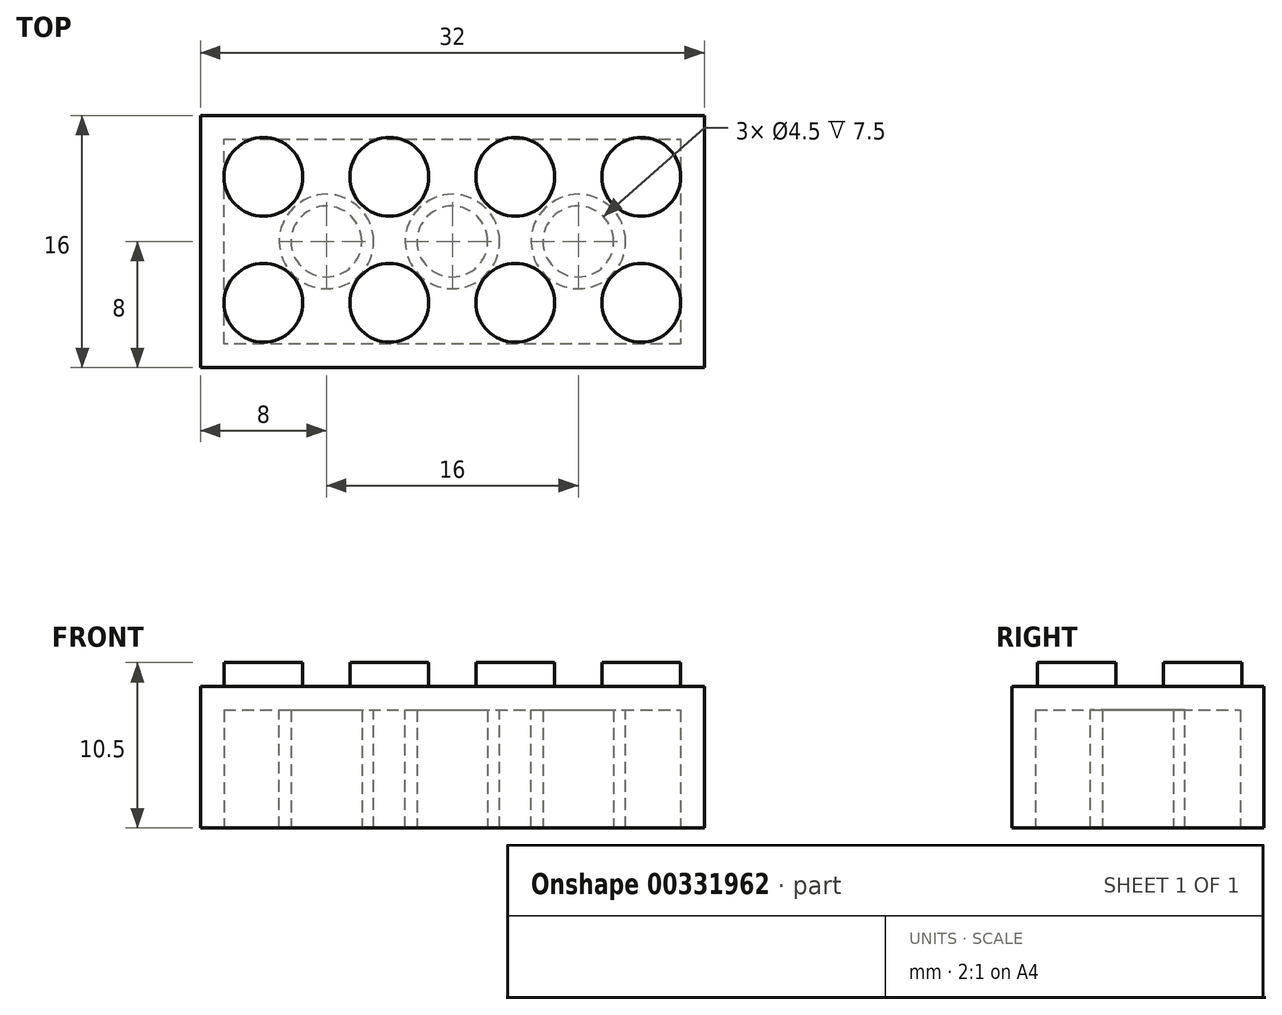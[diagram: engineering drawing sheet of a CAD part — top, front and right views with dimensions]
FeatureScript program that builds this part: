
annotation { "Feature Type Name" : "Feature", "Feature Type Description" : "" }
export const myFeature = defineFeature(function(context is Context, id is Id, definition is map)
    precondition{}
    {
        {
            var Q0;
            Q0=qCreatedBy(makeId("Top.planeOp"),FACE);
            var sketch = newSketch(context, id + "F0", { "sketchPlane" : qUnion([Q0])});
            skLineSegment(sketch, "E0.bottom", {"start": v(0, 0) * mm, "end": v(32, 0) * mm});
            skLineSegment(sketch, "E0.top", {"start": v(0, 16) * mm, "end": v(32, 16) * mm});
            skLineSegment(sketch, "E0.left", {"start": v(0, 0) * mm, "end": v(0, 16) * mm});
            skLineSegment(sketch, "E0.right", {"start": v(32, 0) * mm, "end": v(32, 16) * mm});
            skSolve(sketch);
        }
        {
            var Q0;
            Q0=makeQuery(id+"F0.imprint","IMPRINT",FACE,{"disambiguationData":[TD([[makeQuery(id+"F0.imprint","IMPRINT",EDGE,{"derivedFrom":sQuery(id+"F0.wireOp",EDGE,"E0.bottom")}),1.0]])]});
            extrude(context, id + "F1", {"entities" : qUnion([Q0]), "depth" : 9 * mm});
        }
        {
            var Q0;
            Q0=makeQuery(id+"F1.opExtrude","CAP_FACE",FACE,{"disambiguationData":[OSD([sQuery(id+"F0.wireOp",EDGE,"E0.bottom"),sQuery(id+"F0.wireOp",EDGE,"E0.top"),sQuery(id+"F0.wireOp",EDGE,"E0.left"),sQuery(id+"F0.wireOp",EDGE,"E0.right")])],"isStart":false});
            var sketch = newSketch(context, id + "F2", { "sketchPlane" : qUnion([Q0])});
            skLineSegment(sketch, "E1.left", {"start": v(4, 12.1) * mm, "end": v(4, 4.1) * mm, "construction": true});
            skLineSegment(sketch, "E2", {"start": v(4, 8.1) * mm, "end": v(0, 8.1) * mm, "construction": true});
            skLineSegment(sketch, "E3", {"start": v(16, 16) * mm, "end": v(16, 12) * mm, "construction": true});
            skCircle(sketch, "E4", {"center": v(4, 12.1) * mm, "radius": 2.5 * mm});
            skCircle(sketch, "E5", {"center": v(12, 12.1) * mm, "radius": 2.5 * mm});
            skCircle(sketch, "E6", {"center": v(20, 12.1) * mm, "radius": 2.5 * mm});
            skCircle(sketch, "E7", {"center": v(28, 12.1) * mm, "radius": 2.5 * mm});
            skLineSegment(sketch, "E8", {"start": v(4, 12.1) * mm, "end": v(12, 12.1) * mm, "construction": true});
            skLineSegment(sketch, "E9", {"start": v(12, 12.1) * mm, "end": v(20, 12.1) * mm, "construction": true});
            skLineSegment(sketch, "E10", {"start": v(20, 12.1) * mm, "end": v(28, 12.1) * mm, "construction": true});
            skCircle(sketch, "E11", {"center": v(4, 4.1) * mm, "radius": 2.5 * mm});
            skCircle(sketch, "E12", {"center": v(12, 4.1) * mm, "radius": 2.5 * mm});
            skCircle(sketch, "E13", {"center": v(20, 4.1) * mm, "radius": 2.5 * mm});
            skCircle(sketch, "E14", {"center": v(28, 4.1) * mm, "radius": 2.5 * mm});
            skLineSegment(sketch, "E15", {"start": v(4, 4.1) * mm, "end": v(12, 4.1) * mm, "construction": true});
            skLineSegment(sketch, "E16", {"start": v(12, 4.1) * mm, "end": v(20, 4.1) * mm, "construction": true});
            skLineSegment(sketch, "E17", {"start": v(20, 4.1) * mm, "end": v(28, 4.1) * mm, "construction": true});
            skSolve(sketch);
        }
        {
            var Q0;
            Q0=makeQuery(id+"F2.imprint","IMPRINT",FACE,{"disambiguationData":[TD([[makeQuery(id+"F2.imprint","IMPRINT",EDGE,{"derivedFrom":sQuery(id+"F2.wireOp",EDGE,"E11")}),1.0]])]});
            var Q1;
            Q1=makeQuery(id+"F2.imprint","IMPRINT",FACE,{"disambiguationData":[TD([[makeQuery(id+"F2.imprint","IMPRINT",EDGE,{"derivedFrom":sQuery(id+"F2.wireOp",EDGE,"E4")}),1.0]])]});
            var Q2;
            Q2=makeQuery(id+"F2.imprint","IMPRINT",FACE,{"disambiguationData":[TD([[makeQuery(id+"F2.imprint","IMPRINT",EDGE,{"derivedFrom":sQuery(id+"F2.wireOp",EDGE,"E5")}),1.0]])]});
            var Q3;
            Q3=makeQuery(id+"F2.imprint","IMPRINT",FACE,{"disambiguationData":[TD([[makeQuery(id+"F2.imprint","IMPRINT",EDGE,{"derivedFrom":sQuery(id+"F2.wireOp",EDGE,"E12")}),1.0]])]});
            var Q4;
            Q4=makeQuery(id+"F2.imprint","IMPRINT",FACE,{"disambiguationData":[TD([[makeQuery(id+"F2.imprint","IMPRINT",EDGE,{"derivedFrom":sQuery(id+"F2.wireOp",EDGE,"E6")}),1.0]])]});
            var Q5;
            Q5=makeQuery(id+"F2.imprint","IMPRINT",FACE,{"disambiguationData":[TD([[makeQuery(id+"F2.imprint","IMPRINT",EDGE,{"derivedFrom":sQuery(id+"F2.wireOp",EDGE,"E13")}),1.0]])]});
            var Q6;
            Q6=makeQuery(id+"F2.imprint","IMPRINT",FACE,{"disambiguationData":[TD([[makeQuery(id+"F2.imprint","IMPRINT",EDGE,{"derivedFrom":sQuery(id+"F2.wireOp",EDGE,"E14")}),1.0]])]});
            var Q7;
            Q7=makeQuery(id+"F2.imprint","IMPRINT",FACE,{"disambiguationData":[TD([[makeQuery(id+"F2.imprint","IMPRINT",EDGE,{"derivedFrom":sQuery(id+"F2.wireOp",EDGE,"E7")}),1.0]])]});
            extrude(context, id + "F3", {"entities" : qUnion([Q0, Q1, Q2, Q3, Q4, Q5, Q6, Q7]), "operationType" : NewBodyOperationType.ADD, "depth" : 1.5 * mm});
        }
        {
            var Q0;
            Q0=makeQuery(id+"F1.opExtrude","CAP_FACE",FACE,{"disambiguationData":[OSD([sQuery(id+"F0.wireOp",EDGE,"E0.bottom"),sQuery(id+"F0.wireOp",EDGE,"E0.top"),sQuery(id+"F0.wireOp",EDGE,"E0.left"),sQuery(id+"F0.wireOp",EDGE,"E0.right")])],"isStart":true});
            var sketch = newSketch(context, id + "F4", { "sketchPlane" : qUnion([Q0])});
            skLineSegment(sketch, "E18.0", {"start": v(1.5, -14.5) * mm, "end": v(30.5, -14.5) * mm});
            skLineSegment(sketch, "E18.1", {"start": v(1.5, -1.5) * mm, "end": v(1.5, -14.5) * mm});
            skLineSegment(sketch, "E18.2", {"start": v(30.5, -1.5) * mm, "end": v(1.5, -1.5) * mm});
            skLineSegment(sketch, "E18.3", {"start": v(30.5, -14.5) * mm, "end": v(30.5, -1.5) * mm});
            skSolve(sketch);
        }
        {
            var Q0;
            Q0 = qSketchRegion(id + "F4", true);
            var Q1;
            Q1=makeQuery(id+"F4.imprint","IMPRINT",FACE,{"disambiguationData":[TD([[makeQuery(id+"F4.imprint","IMPRINT",EDGE,{"derivedFrom":sQuery(id+"F4.wireOp",EDGE,"E18.0")}),1.0]])]});
            extrude(context, id + "F5", {"entities" : qUnion([Q0, Q1]), "operationType" : NewBodyOperationType.REMOVE, "oppositeDirection" : true, "depth" : 7.5 * mm});
        }
        {
            var Q0;
            Q0=makeQuery(id+"F5.boolean.opBoolean","COPY",FACE,{"derivedFrom":makeQuery(id+"F5.opExtrude","CAP_FACE",FACE,{"disambiguationData":[OSD([sQuery(id+"F4.wireOp",EDGE,"E18.0"),sQuery(id+"F4.wireOp",EDGE,"E18.1"),sQuery(id+"F4.wireOp",EDGE,"E18.2"),sQuery(id+"F4.wireOp",EDGE,"E18.3")])],"isStart":false})});
            var sketch = newSketch(context, id + "F6", { "sketchPlane" : qUnion([Q0])});
            skLineSegment(sketch, "E19", {"start": v(1.5, -8) * mm, "end": v(30.5, -8) * mm, "construction": true});
            skCircle(sketch, "E20", {"center": v(8, -8) * mm, "radius": 3 * mm});
            skCircle(sketch, "E21", {"center": v(16, -8) * mm, "radius": 3 * mm});
            skCircle(sketch, "E22", {"center": v(24, -8) * mm, "radius": 3 * mm});
            skSolve(sketch);
        }
        {
            var Q0;
            Q0=makeQuery(id+"F6.imprint","IMPRINT",FACE,{"disambiguationData":[TD([[makeQuery(id+"F6.imprint","IMPRINT",EDGE,{"derivedFrom":sQuery(id+"F6.wireOp",EDGE,"E20")}),1.0]])]});
            var Q1;
            Q1=makeQuery(id+"F6.imprint","IMPRINT",FACE,{"disambiguationData":[TD([[makeQuery(id+"F6.imprint","IMPRINT",EDGE,{"derivedFrom":sQuery(id+"F6.wireOp",EDGE,"E21")}),1.0]])]});
            var Q2;
            Q2=makeQuery(id+"F6.imprint","IMPRINT",FACE,{"disambiguationData":[TD([[makeQuery(id+"F6.imprint","IMPRINT",EDGE,{"derivedFrom":sQuery(id+"F6.wireOp",EDGE,"E22")}),1.0]])]});
            extrude(context, id + "F7", {"entities" : qUnion([Q0, Q1, Q2]), "operationType" : NewBodyOperationType.ADD, "depth" : 7.5 * mm});
        }
        {
            var Q0;
            Q0=makeQuery(id+"F7.opExtrude","CAP_FACE",FACE,{"disambiguationData":[OSD([sQuery(id+"F6.wireOp",EDGE,"E20")])],"isStart":false});
            var sketch = newSketch(context, id + "F8", { "sketchPlane" : qUnion([Q0])});
            skCircle(sketch, "E23.0", {"center": v(16, -8) * mm, "radius": 2.25 * mm});
            skCircle(sketch, "E24.0", {"center": v(8, -8) * mm, "radius": 2.25 * mm});
            skCircle(sketch, "E25.0", {"center": v(24, -8) * mm, "radius": 2.25 * mm});
            skSolve(sketch);
        }
        {
            var Q0;
            Q0=makeQuery(id+"F8.imprint","IMPRINT",FACE,{"disambiguationData":[TD([[makeQuery(id+"F8.imprint","IMPRINT",EDGE,{"derivedFrom":sQuery(id+"F8.wireOp",EDGE,"E24.0")}),1.0]])]});
            var Q1;
            Q1=makeQuery(id+"F8.imprint","IMPRINT",FACE,{"disambiguationData":[TD([[makeQuery(id+"F8.imprint","IMPRINT",EDGE,{"derivedFrom":sQuery(id+"F8.wireOp",EDGE,"E23.0")}),1.0]])]});
            var Q2;
            Q2=makeQuery(id+"F8.imprint","IMPRINT",FACE,{"disambiguationData":[TD([[makeQuery(id+"F8.imprint","IMPRINT",EDGE,{"derivedFrom":sQuery(id+"F8.wireOp",EDGE,"E25.0")}),1.0]])]});
            extrude(context, id + "F9", {"entities" : qUnion([Q0, Q1, Q2]), "operationType" : NewBodyOperationType.REMOVE, "oppositeDirection" : true, "depth" : 7.5 * mm});
        }
    });
